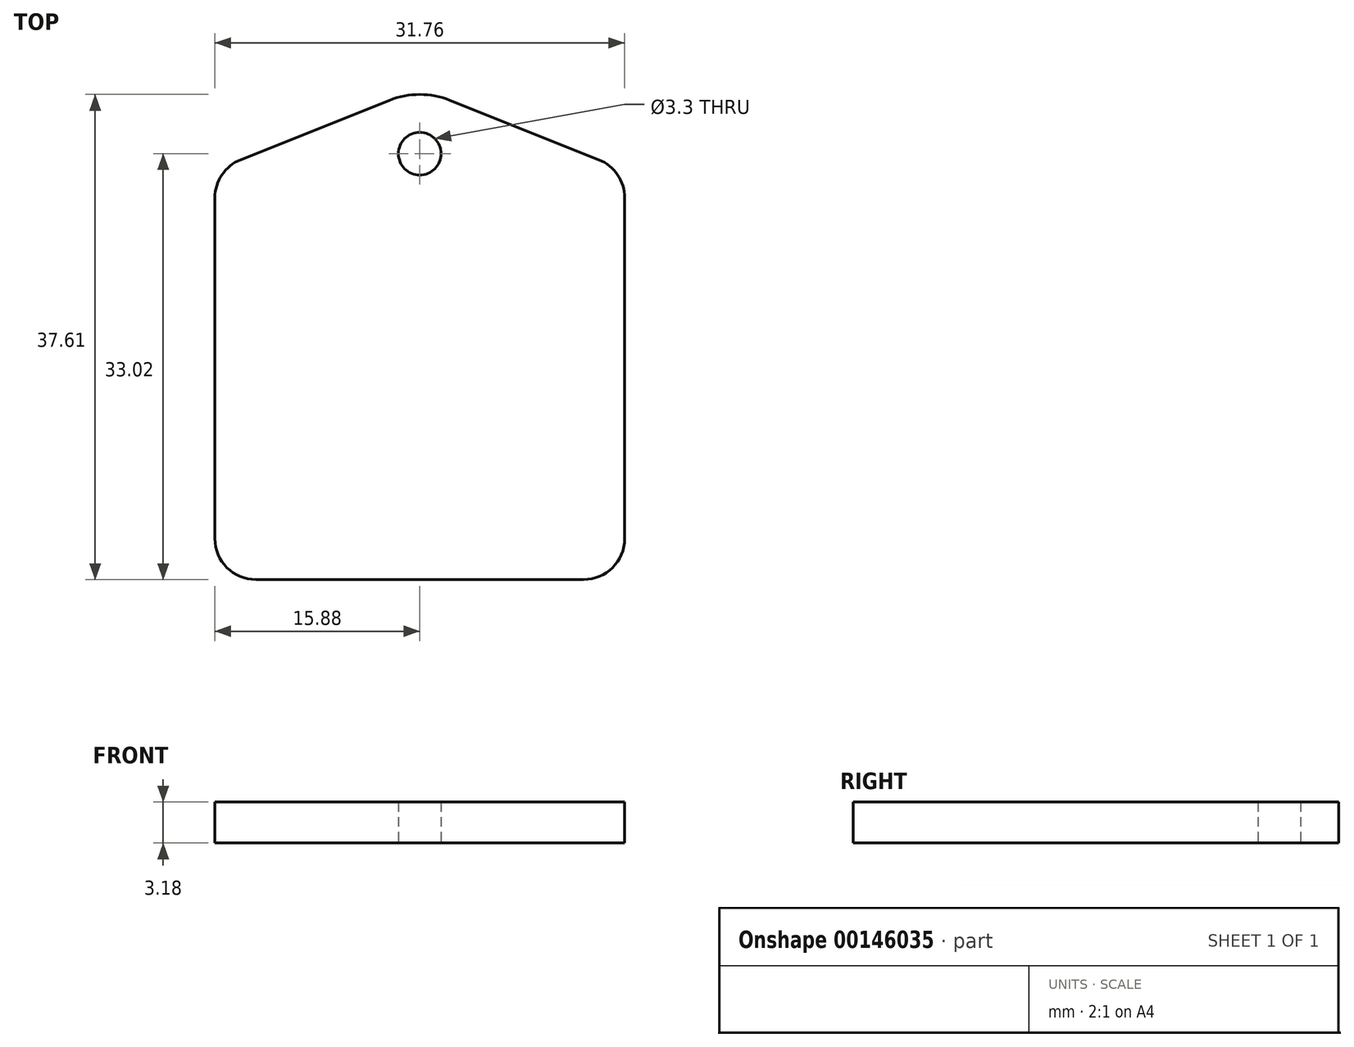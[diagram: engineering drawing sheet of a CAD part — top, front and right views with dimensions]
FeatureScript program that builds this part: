
annotation { "Feature Type Name" : "Feature", "Feature Type Description" : "" }
export const myFeature = defineFeature(function(context is Context, id is Id, definition is map)
    precondition{}
    {
        {
            var Q0;
            Q0=qCreatedBy(makeId("Top.planeOp"),FACE);
            var sketch = newSketch(context, id + "F0", { "sketchPlane" : qUnion([Q0])});
            skLineSegment(sketch, "E0", {"start": v(0, 0) * mm, "end": v(0, 66.04) * mm, "construction": true});
            skLineSegment(sketch, "E1.bottom", {"start": v(-12.7, 0) * mm, "end": v(12.7, 0) * mm});
            skLineSegment(sketch, "E1.left", {"start": v(-15.88, 3.18) * mm, "end": v(-15.88, 29.6) * mm});
            skLineSegment(sketch, "E1.right", {"start": v(15.88, 3.18) * mm, "end": v(15.88, 29.6) * mm});
            skLineSegment(sketch, "E2", {"start": v(-13.88, 32.55) * mm, "end": v(-2.36, 37.16) * mm});
            skLineSegment(sketch, "E3", {"start": v(2.36, 37.16) * mm, "end": v(13.88, 32.55) * mm});
            skPoint(sketch, "E4.visualSharp", {"position": v(-15.88, 0) * mm});
            skArc(sketch, "E4.filletArc", {"start": v(-15.88, 3.17) * mm, "mid": v(-14.95, 0.93) * mm, "end": v(-12.7, 0) * mm});
            skPoint(sketch, "E5.visualSharp", {"position": v(15.88, 0) * mm});
            skArc(sketch, "E5.filletArc", {"start": v(12.7, 0) * mm, "mid": v(14.95, 0.93) * mm, "end": v(15.88, 3.18) * mm});
            skPoint(sketch, "E6.visualSharp", {"position": v(15.88, 31.75) * mm});
            skArc(sketch, "E6.filletArc", {"start": v(15.88, 29.6) * mm, "mid": v(15.33, 31.38) * mm, "end": v(13.88, 32.55) * mm});
            skPoint(sketch, "E7.visualSharp", {"position": v(-15.88, 31.75) * mm});
            skArc(sketch, "E7.filletArc", {"start": v(-13.88, 32.55) * mm, "mid": v(-15.33, 31.38) * mm, "end": v(-15.88, 29.6) * mm});
            skPoint(sketch, "E8.visualSharp", {"position": v(0, 38.1) * mm});
            skArc(sketch, "E8.filletArc", {"start": v(2.36, 37.16) * mm, "mid": v(0, 37.61) * mm, "end": v(-2.36, 37.16) * mm});
            skCircle(sketch, "E9", {"center": v(0, 33.02) * mm, "radius": 1.65 * mm});
            skSolve(sketch);
        }
        {
            var Q0;
            Q0=makeQuery(id+"F0.imprint","IMPRINT",FACE,{"disambiguationData":[TD([[makeQuery(id+"F0.imprint","IMPRINT",EDGE,{"derivedFrom":sQuery(id+"F0.wireOp",EDGE,"E1.bottom")}),1.0]])]});
            extrude(context, id + "F1", {"entities" : qUnion([Q0]), "depth" : 3.17 * mm});
        }
    });
